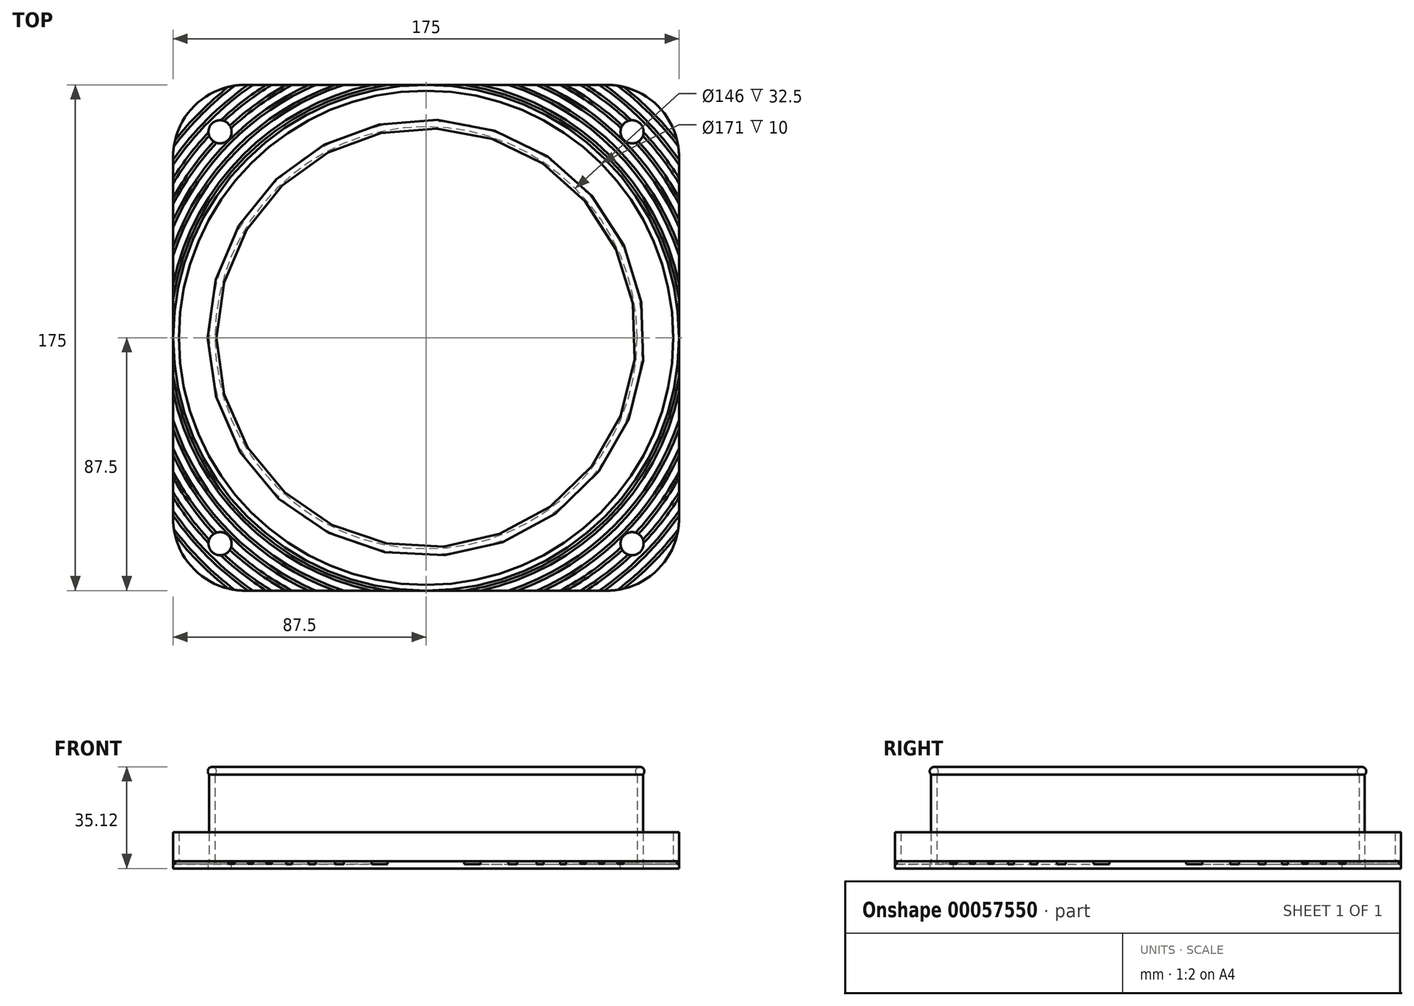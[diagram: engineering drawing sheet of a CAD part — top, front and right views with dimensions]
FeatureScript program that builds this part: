
annotation { "Feature Type Name" : "Feature", "Feature Type Description" : "" }
export const myFeature = defineFeature(function(context is Context, id is Id, definition is map)
    precondition{}
    {
        {
            var Q0;
            Q0=qCreatedBy(makeId("Top.planeOp"),FACE);
            var sketch = newSketch(context, id + "F0", { "sketchPlane" : qUnion([Q0])});
            skLineSegment(sketch, "E0.rect.bottom", {"start": v(87.5, -87.5) * mm, "end": v(-87.5, -87.5) * mm});
            skLineSegment(sketch, "E0.rect.top", {"start": v(87.5, 87.5) * mm, "end": v(-87.5, 87.5) * mm});
            skLineSegment(sketch, "E0.rect.left", {"start": v(87.5, -87.5) * mm, "end": v(87.5, 87.5) * mm});
            skLineSegment(sketch, "E0.rect.right", {"start": v(-87.5, -87.5) * mm, "end": v(-87.5, 87.5) * mm});
            skPoint(sketch, "E0.rect.middle", {"position": v(0, 0) * mm});
            skCircle(sketch, "E1", {"center": v(0, 0) * mm, "radius": 73 * mm});
            skSolve(sketch);
        }
        {
            var Q0;
            Q0=makeQuery(id+"F0.imprint","IMPRINT",FACE,{"disambiguationData":[TD([[makeQuery(id+"F0.imprint","IMPRINT",EDGE,{"derivedFrom":sQuery(id+"F0.wireOp",EDGE,"E0.rect.bottom")}),-1.0]])]});
            extrude(context, id + "F1", {"entities" : qUnion([Q0]), "depth" : 2.5 * mm});
        }
        {
            var Q0;
            Q0=makeQuery(id+"F1.opExtrude","CAP_FACE",FACE,{"disambiguationData":[OSD([sQuery(id+"F0.wireOp",EDGE,"E0.rect.bottom"),sQuery(id+"F0.wireOp",EDGE,"E0.rect.top"),sQuery(id+"F0.wireOp",EDGE,"E0.rect.left"),sQuery(id+"F0.wireOp",EDGE,"E0.rect.right"),sQuery(id+"F0.wireOp",EDGE,"E1")])],"isStart":false});
            var sketch = newSketch(context, id + "F2", { "sketchPlane" : qUnion([Q0])});
            skCircle(sketch, "E2", {"center": v(0, 0) * mm, "radius": 75 * mm});
            skSolve(sketch);
        }
        {
            var Q0;
            Q0=makeQuery(id+"F2.imprint","IMPRINT",FACE,{"disambiguationData":[TD([[makeQuery(id+"F2.imprint","IMPRINT",EDGE,{"derivedFrom":sQuery(id+"F2.wireOp",EDGE,"E2")}),1.0]])]});
            extrude(context, id + "F3", {"entities" : qUnion([Q0]), "operationType" : NewBodyOperationType.ADD, "depth" : 30 * mm});
        }
        {
            var Q0;
            Q0=qCreatedBy(makeId("Right.planeOp"),FACE);
            var sketch = newSketch(context, id + "F4", { "sketchPlane" : qUnion([Q0])});
            skLineSegment(sketch, "E3", {"start": v(75, 32.5) * mm, "end": v(75, 2.5) * mm});
            skLineSegment(sketch, "E4", {"start": v(-75, 2.5) * mm, "end": v(-75, 32.5) * mm});
            skLineSegment(sketch, "E5", {"start": v(73, 32.5) * mm, "end": v(73, 0) * mm});
            skLineSegment(sketch, "E6", {"start": v(-73, 0) * mm, "end": v(-73, 32.5) * mm});
            skLineSegment(sketch, "E7", {"start": v(-73, 32.5) * mm, "end": v(-75, 32.5) * mm});
            skLineSegment(sketch, "E8", {"start": v(75, 32.5) * mm, "end": v(73, 32.5) * mm});
            skCircle(sketch, "E9", {"center": v(-74, 33.62) * mm, "radius": 1.5 * mm});
            skPoint(sketch, "E9.centerSnap0", {"position": v(-74, 32.5) * mm});
            skLineSegment(sketch, "E10", {"start": v(0, 0) * mm, "end": v(0, 32.78) * mm});
            skSolve(sketch);
        }
        {
            var Q0;
            {var subQ0=sQuery(id+"F4.wireOp",EDGE,"E7");Q0=makeQuery(id+"F4.imprint","IMPRINT",FACE,{"disambiguationData":[TD([[makeQuery(id+"F4.imprint","IMPRINT",EDGE,{"derivedFrom":subQ0}),-1.0]])]});}
            var Q1;
            Q1=sQuery(id+"F4.wireOp",EDGE,"E10");
            revolve(context, id + "F5", {"entities" : qUnion([Q0]), "axis" : qUnion([Q1]), "revolveType" : RevolveType.FULL});
        }
        {
            var Q0;
            Q0=makeQuery(id+"F1.opExtrude","SWEPT_EDGE",EDGE,{"disambiguationData":[OSD([sQuery(id+"F0.wireOp",EDGE,"E0.rect.bottom"),sQuery(id+"F0.wireOp",EDGE,"E0.rect.right")])]});
            var Q1;
            Q1=makeQuery(id+"F1.opExtrude","SWEPT_EDGE",EDGE,{"disambiguationData":[OSD([sQuery(id+"F0.wireOp",EDGE,"E0.rect.bottom"),sQuery(id+"F0.wireOp",EDGE,"E0.rect.left")])]});
            var Q2;
            Q2=makeQuery(id+"F1.opExtrude","SWEPT_EDGE",EDGE,{"disambiguationData":[OSD([sQuery(id+"F0.wireOp",EDGE,"E0.rect.top"),sQuery(id+"F0.wireOp",EDGE,"E0.rect.left")])]});
            var Q3;
            Q3=makeQuery(id+"F1.opExtrude","SWEPT_EDGE",EDGE,{"disambiguationData":[OSD([sQuery(id+"F0.wireOp",EDGE,"E0.rect.top"),sQuery(id+"F0.wireOp",EDGE,"E0.rect.right")])]});
            fillet(context, id + "F6", {"entities" : qUnion([Q0, Q1, Q2, Q3]), "radius" : 25 * mm, "tangentPropagation" : true, "allowEdgeOverflow" : false});
        }
        {
            var Q0;
            Q0=makeQuery(id+"F1.opExtrude","CAP_FACE",FACE,{"disambiguationData":[OSD([sQuery(id+"F0.wireOp",EDGE,"E0.rect.bottom"),sQuery(id+"F0.wireOp",EDGE,"E0.rect.top"),sQuery(id+"F0.wireOp",EDGE,"E0.rect.left"),sQuery(id+"F0.wireOp",EDGE,"E0.rect.right"),sQuery(id+"F0.wireOp",EDGE,"E1")])],"isStart":false});
            var sketch = newSketch(context, id + "F7", { "sketchPlane" : qUnion([Q0])});
            skLineSegment(sketch, "E11.rect.bottom", {"start": v(-71.25, 71.25) * mm, "end": v(71.25, 71.25) * mm});
            skLineSegment(sketch, "E11.rect.top", {"start": v(-71.25, -71.25) * mm, "end": v(71.25, -71.25) * mm});
            skLineSegment(sketch, "E11.rect.left", {"start": v(-71.25, 71.25) * mm, "end": v(-71.25, -71.25) * mm});
            skLineSegment(sketch, "E11.rect.right", {"start": v(71.25, 71.25) * mm, "end": v(71.25, -71.25) * mm});
            skPoint(sketch, "E11.rect.middle", {"position": v(0, 0) * mm});
            skSolve(sketch);
        }
        {
            var Q0;
            Q0=sQuery(id+"F7.wireOp",VERTEX,"E11.rect.left.start");
            var Q1;
            Q1=sQuery(id+"F7.wireOp",VERTEX,"E11.rect.right.start");
            var Q2;
            Q2=sQuery(id+"F7.wireOp",VERTEX,"E11.rect.top.end");
            var Q3;
            Q3=sQuery(id+"F7.wireOp",VERTEX,"E11.rect.left.end");
            var Q4;
            Q4=makeQuery(id+"F1.opExtrude","SWEPT_BODY",BODY,{"disambiguationData":[OSD([sQuery(id+"F0.wireOp",EDGE,"E0.rect.bottom"),sQuery(id+"F0.wireOp",EDGE,"E0.rect.top"),sQuery(id+"F0.wireOp",EDGE,"E0.rect.left"),sQuery(id+"F0.wireOp",EDGE,"E0.rect.right"),sQuery(id+"F0.wireOp",EDGE,"E1")])]});
            hole(context, id + "F8", {"style" : HoleStyle.SIMPLE, "holeDiameter" : 8 * mm, "endStyle" : HoleEndStyle.THROUGH, "locations" : qUnion([Q0, Q1, Q2, Q3]), "scope" : qUnion([Q4])});
        }
        {
            var Q0;
            Q0=makeQuery(id+"F1.opExtrude","CAP_FACE",FACE,{"disambiguationData":[OSD([sQuery(id+"F0.wireOp",EDGE,"E0.rect.bottom"),sQuery(id+"F0.wireOp",EDGE,"E0.rect.top"),sQuery(id+"F0.wireOp",EDGE,"E0.rect.left"),sQuery(id+"F0.wireOp",EDGE,"E0.rect.right"),sQuery(id+"F0.wireOp",EDGE,"E1")])],"isStart":false});
            var sketch = newSketch(context, id + "F9", { "sketchPlane" : qUnion([Q0])});
            skCircle(sketch, "E12", {"center": v(0, 0) * mm, "radius": 87.5 * mm});
            skCircle(sketch, "E13", {"center": v(0, 0) * mm, "radius": 85.5 * mm});
            skSolve(sketch);
        }
        {
            var Q0;
            Q0 = qSketchRegion(id + "F9", true);
            extrude(context, id + "F10", {"entities" : qUnion([Q0]), "operationType" : NewBodyOperationType.ADD, "depth" : 10 * mm});
        }
        {
            var Q0;
            Q0=qCreatedBy(makeId("Front.planeOp"),FACE);
            var sketch = newSketch(context, id + "F11", { "sketchPlane" : qUnion([Q0])});
            skLineSegment(sketch, "E14.bottom", {"start": v(-88.5, 3.17) * mm, "end": v(-89.5, 3.17) * mm});
            skLineSegment(sketch, "E14.top", {"start": v(-88.5, 1.5) * mm, "end": v(-89.5, 1.5) * mm});
            skLineSegment(sketch, "E14.left", {"start": v(-88.5, 3.17) * mm, "end": v(-88.5, 1.5) * mm});
            skLineSegment(sketch, "E14.right", {"start": v(-89.5, 3.17) * mm, "end": v(-89.5, 1.5) * mm});
            skLineSegment(sketch, "E15.direction1", {"start": v(-89.5, 1.5) * mm, "end": v(-64.5, 1.5) * mm, "construction": true});
            skLineSegment(sketch, "E16.1.0.0", {"start": v(-92, 3.18) * mm, "end": v(-93, 3.18) * mm});
            skLineSegment(sketch, "E16.1.0.1", {"start": v(-93, 3.18) * mm, "end": v(-93, 1.51) * mm});
            skLineSegment(sketch, "E16.1.0.2", {"start": v(-92, 3.18) * mm, "end": v(-92, 1.51) * mm});
            skLineSegment(sketch, "E16.1.0.3", {"start": v(-92, 1.51) * mm, "end": v(-93, 1.51) * mm});
            skLineSegment(sketch, "E16.2.0.0", {"start": v(-95.5, 3.19) * mm, "end": v(-96.5, 3.19) * mm});
            skLineSegment(sketch, "E16.2.0.1", {"start": v(-96.5, 3.19) * mm, "end": v(-96.5, 1.52) * mm});
            skLineSegment(sketch, "E16.2.0.2", {"start": v(-95.5, 3.19) * mm, "end": v(-95.5, 1.52) * mm});
            skLineSegment(sketch, "E16.2.0.3", {"start": v(-95.5, 1.52) * mm, "end": v(-96.5, 1.52) * mm});
            skLineSegment(sketch, "E16.3.0.0", {"start": v(-99, 3.2) * mm, "end": v(-100, 3.2) * mm});
            skLineSegment(sketch, "E16.3.0.1", {"start": v(-100, 3.2) * mm, "end": v(-100, 1.53) * mm});
            skLineSegment(sketch, "E16.3.0.2", {"start": v(-99, 3.2) * mm, "end": v(-99, 1.53) * mm});
            skLineSegment(sketch, "E16.3.0.3", {"start": v(-99, 1.53) * mm, "end": v(-100, 1.53) * mm});
            skLineSegment(sketch, "E16.4.0.0", {"start": v(-102.5, 3.21) * mm, "end": v(-103.5, 3.21) * mm});
            skLineSegment(sketch, "E16.4.0.1", {"start": v(-103.5, 3.21) * mm, "end": v(-103.5, 1.54) * mm});
            skLineSegment(sketch, "E16.4.0.2", {"start": v(-102.5, 3.21) * mm, "end": v(-102.5, 1.54) * mm});
            skLineSegment(sketch, "E16.4.0.3", {"start": v(-102.5, 1.54) * mm, "end": v(-103.5, 1.54) * mm});
            skLineSegment(sketch, "E16.direction1", {"start": v(-89.5, 1.5) * mm, "end": v(-93, 1.51) * mm, "construction": true});
            skLineSegment(sketch, "E17", {"start": v(0, 0) * mm, "end": v(0, 37.49) * mm});
            skLineSegment(sketch, "E18.0.5.0", {"start": v(-106, 3.22) * mm, "end": v(-107, 3.22) * mm});
            skLineSegment(sketch, "E18.3.5.0", {"start": v(-107, 3.22) * mm, "end": v(-107, 1.56) * mm});
            skLineSegment(sketch, "E18.6.5.0", {"start": v(-106, 3.22) * mm, "end": v(-106, 1.56) * mm});
            skLineSegment(sketch, "E18.9.5.0", {"start": v(-106, 1.56) * mm, "end": v(-107, 1.56) * mm});
            skLineSegment(sketch, "E18.0.6.0", {"start": v(-109.5, 3.23) * mm, "end": v(-110.5, 3.23) * mm});
            skLineSegment(sketch, "E18.3.6.0", {"start": v(-110.5, 3.23) * mm, "end": v(-110.5, 1.57) * mm});
            skLineSegment(sketch, "E18.6.6.0", {"start": v(-109.5, 3.23) * mm, "end": v(-109.5, 1.57) * mm});
            skLineSegment(sketch, "E18.9.6.0", {"start": v(-109.5, 1.57) * mm, "end": v(-110.5, 1.57) * mm});
            skSolve(sketch);
        }
        {
            var Q0;
            Q0=makeQuery(id+"F11.imprint","IMPRINT",FACE,{"disambiguationData":[TD([[makeQuery(id+"F11.imprint","IMPRINT",EDGE,{"derivedFrom":sQuery(id+"F11.wireOp",EDGE,"E14.bottom")}),1.0]])]});
            var Q1;
            Q1=makeQuery(id+"F11.imprint","IMPRINT",FACE,{"disambiguationData":[TD([[makeQuery(id+"F11.imprint","IMPRINT",EDGE,{"derivedFrom":sQuery(id+"F11.wireOp",EDGE,"E16.1.0.0")}),1.0]])]});
            var Q2;
            Q2=makeQuery(id+"F11.imprint","IMPRINT",FACE,{"disambiguationData":[TD([[makeQuery(id+"F11.imprint","IMPRINT",EDGE,{"derivedFrom":sQuery(id+"F11.wireOp",EDGE,"E16.2.0.0")}),1.0]])]});
            var Q3;
            Q3=makeQuery(id+"F11.imprint","IMPRINT",FACE,{"disambiguationData":[TD([[makeQuery(id+"F11.imprint","IMPRINT",EDGE,{"derivedFrom":sQuery(id+"F11.wireOp",EDGE,"E16.3.0.0")}),1.0]])]});
            var Q4;
            Q4=makeQuery(id+"F11.imprint","IMPRINT",FACE,{"disambiguationData":[TD([[makeQuery(id+"F11.imprint","IMPRINT",EDGE,{"derivedFrom":sQuery(id+"F11.wireOp",EDGE,"E16.4.0.0")}),1.0]])]});
            var Q5;
            Q5=makeQuery(id+"F11.imprint","IMPRINT",FACE,{"disambiguationData":[TD([[makeQuery(id+"F11.imprint","IMPRINT",EDGE,{"derivedFrom":sQuery(id+"F11.wireOp",EDGE,"E18.0.5.0")}),1.0]])]});
            var Q6;
            Q6=makeQuery(id+"F11.imprint","IMPRINT",FACE,{"disambiguationData":[TD([[makeQuery(id+"F11.imprint","IMPRINT",EDGE,{"derivedFrom":sQuery(id+"F11.wireOp",EDGE,"E18.0.6.0")}),1.0]])]});
            var Q7;
            Q7=sQuery(id+"F11.wireOp",EDGE,"E17");
            revolve(context, id + "F12", {"operationType" : NewBodyOperationType.REMOVE, "entities" : qUnion([Q0, Q1, Q2, Q3, Q4, Q5, Q6]), "axis" : qUnion([Q7]), "revolveType" : RevolveType.FULL});
        }
    });
